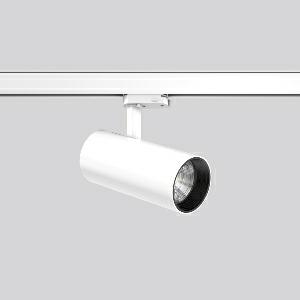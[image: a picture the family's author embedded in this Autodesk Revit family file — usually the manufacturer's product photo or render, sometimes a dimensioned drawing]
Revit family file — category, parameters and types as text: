
# Revit family: deecos_s_mini_742198_002_1_3c05
name_source: partatom
category: Lighting Fixtures
units: mm (PartAtom-declared; Revit-internal decimal feet)

## family parameters
Cut with Voids When Loaded = No
Host = Face
Light Source = No
Part Type = Normal
Room Calculation Point = No
Round Connector Dimension = Use Diameter
Shared = No

## types (1)
- DEECOS S mini (1 x LED Modul 940, 2400 lm, 4000)
    Apparent Load = 20 VA
    Approval mark = CE
    CIE Flux Codes = 99 100 100 100 100
    Color Rendering = 92
    Color Temperature = 4000
    Default Elevation = 1800 mm
    Description = Series: DEECOS S mini
LED surface-mounted projector in modern design with no visible cooling ribs. Housing: die-cast aluminium, powder-coated. Rotation range: 356°. Swivel range: 90°. Black plastic ring and recessed LED to prevent glare from the side. Optical assembly with lens made of plastic (polycarbonate) for the best homogeneous light distribution - can be changed without tools. Best colour rendering index Ra>90. With multi adaptor for 3-circuit tracks 230 V. Suitable for Track on ceiling, Wall track. High quality converter without flickering and stroboscopic effect. The following accessories can be mounted without use of tools: interchangeable lenses, decorative glasses, honeycomb louvre, clear and frosted diffusers, white interchangeable plastic ring. 
Colour: traffic white, matt (RAL 9016)
Diameter: 87 mm
Height: 214 mm
Lamp: LED
Socket: without socket
Colour temperature: 4000K
Colour rendering index (CRI): 92
System power: 20 W
Rated luminous flux: 2400 lm
Luminous efficiency: 120 lm/W
Control gear: Regulated power supply
Protection class: I
Type of protection: IP 20
    Height = 214 mm
    Lamp = 1 x LED Modul 940
    Lamp Light Flux = 2400 lm
    Lamp count = 1
    Length = 87 mm
    Lifetime = 50000 h
    Luminous efficacy = 120 lm/W
    Manufacturer = RZB
    ModVariant = No
    Model = 742198.002.1
    Mounting Place = Ceiling
    Mounting Type = Rail mounted
    Number of Poles = 1
    OnlyDefault = Yes
    Power Factor = 1
    Product Name = DEECOS S mini
    Product group = Track mounted projectors
    ProductGroupID = 301
    Protection Class = Protection class I
    Protection Degree = IP 20
    RLX_Detail_Level = 1
    RLX_Emergency_Light_Flux = 0 lm
    RLX_Emergency_Type = 0
    RLX_Emergency_Type_DB = No
    RlxData = <blob elided: 35173 chars, md5=8fee5274>
    Socket = socket
    Standby Power = 0 W
    System Light Flux = 2400 lm
    System Power = 20 W
    Type Comments = Product without accessories
    Type Image = 741930.002.jpg
    URL = http://relux.com
    VarID = ---
    Voltage = 230 V
    Voltage Range = 220-240 V
    Weight = 0.00 kg
    Width = 0 mm  [stored 0 ft]

note: [stored X ft] marks values corroborated as IEEE doubles in the binary element streams (Revit-internal decimal feet)

## geometry (parser evidence)
native form markers: Blend x4, Sweep x11
no freeform markers — native parametric forms only
